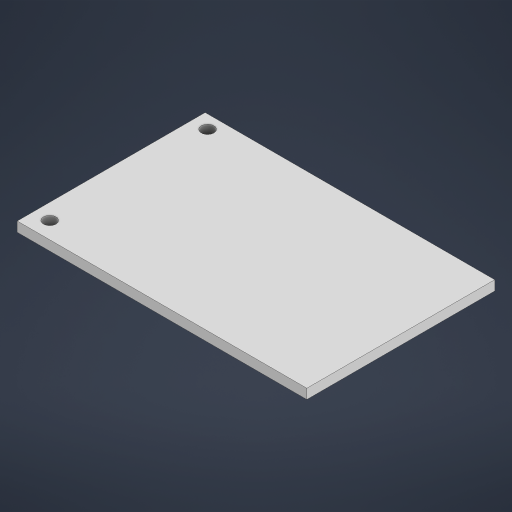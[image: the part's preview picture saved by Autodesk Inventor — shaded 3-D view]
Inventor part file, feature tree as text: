
AUTODESK INVENTOR PART (.ipt)
format: ipt  version: 2023 (Build 270158000, 158)  size: 165,888 bytes
history: native  units: mm
features: sketch x2, extrude x1, hole x1
ambient origin geometry x8: Origin, YZ Plane, XZ Plane, XY Plane, X Axis, Y Axis, Z Axis, Center Point
bodies: Solid1 (feature_tree)
feature tree (4):
  extrude  "Extrusion1"  Depth=30.84mm
  hole  "Hole1"  [1 undecoded]
  sketch  "Sketch1"  dims[d0=47.53mm d1=30.84mm]
  sketch  "Sketch2"  dims[d2=1.6mm d3=0.0mm d4=25.91mm d5=2.19mm d6=2.74mm d7=2.59mm d8=2.08mm d9=6.0mm d10=4.0mm d11=2.0mm d12=90.0deg d13=8.0mm d14=20.594885mm]
note: 1 required parameter value undecoded (feature->parameter linkage not recoverable at this tier; creation-order binding heuristic only, values carry confidence <= 0.55)
